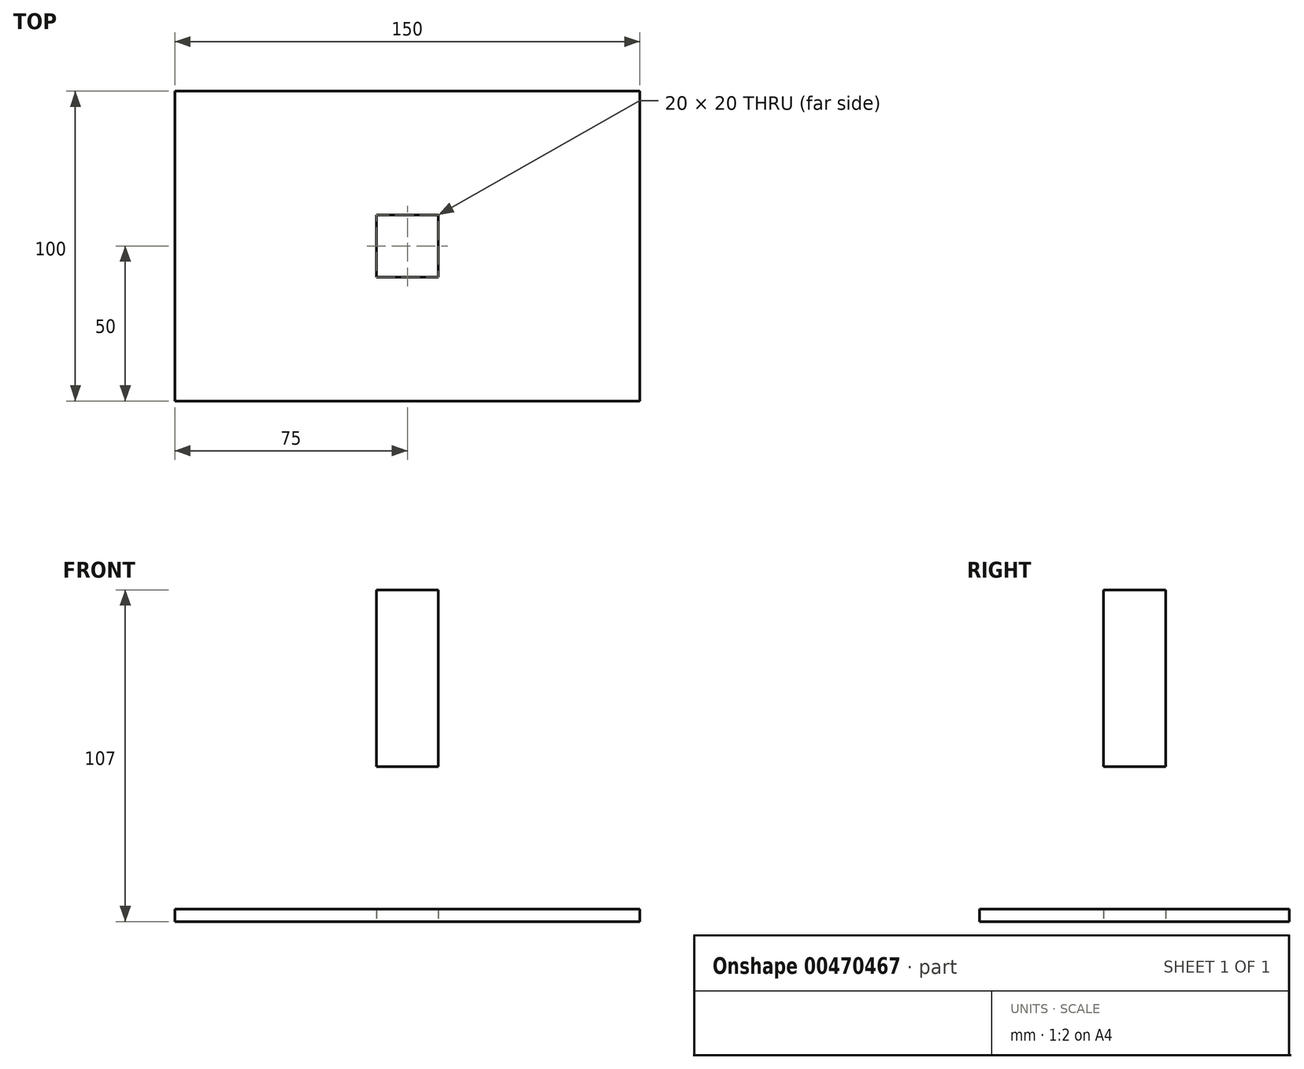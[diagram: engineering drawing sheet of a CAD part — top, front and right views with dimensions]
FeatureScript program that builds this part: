
annotation { "Feature Type Name" : "Feature", "Feature Type Description" : "" }
export const myFeature = defineFeature(function(context is Context, id is Id, definition is map)
    precondition{}
    {
        {
            var Q0;
            Q0=qCreatedBy(makeId("Top.planeOp"),FACE);
            var sketch = newSketch(context, id + "F0", { "sketchPlane" : qUnion([Q0])});
            skLineSegment(sketch, "E0.bottom", {"start": v(0, 0) * mm, "end": v(150, 0) * mm});
            skLineSegment(sketch, "E0.top", {"start": v(0, 100) * mm, "end": v(150, 100) * mm});
            skLineSegment(sketch, "E0.left", {"start": v(0, 0) * mm, "end": v(0, 100) * mm});
            skLineSegment(sketch, "E0.right", {"start": v(150, 0) * mm, "end": v(150, 100) * mm});
            skPoint(sketch, "E1.centerSnap0", {"position": v(0, 50) * mm});
            skPoint(sketch, "E1.centerSnap1", {"position": v(75, 0) * mm});
            skLineSegment(sketch, "E2.bottom", {"start": v(85, 60) * mm, "end": v(65, 60) * mm});
            skLineSegment(sketch, "E2.top", {"start": v(85, 40) * mm, "end": v(65, 40) * mm});
            skLineSegment(sketch, "E2.left", {"start": v(85, 60) * mm, "end": v(85, 40) * mm});
            skLineSegment(sketch, "E2.right", {"start": v(65, 60) * mm, "end": v(65, 40) * mm});
            skPoint(sketch, "E2.middle", {"position": v(75, 50) * mm});
            skPoint(sketch, "E2.middle.positionSnap0", {"position": v(75, 100) * mm});
            skPoint(sketch, "E2.centerSnap0", {"position": v(75, 100) * mm});
            skSolve(sketch);
        }
        {
            var Q0;
            Q0=makeQuery(id+"F0.imprint","IMPRINT",FACE,{"disambiguationData":[TD([[makeQuery(id+"F0.imprint","IMPRINT",EDGE,{"derivedFrom":sQuery(id+"F0.wireOp",EDGE,"E0.bottom")}),1.0]])]});
            extrude(context, id + "F1", {"entities" : qUnion([Q0]), "depth" : 4 * mm});
        }
        {
            var Q0;
            Q0=qCreatedBy(makeId("Top.planeOp"),FACE);
            cPlane(context, id + "F2", {"entities" : qUnion([Q0]), "cplaneType" : CPlaneType.OFFSET, "offset" : 50 * mm, "width" : 150 * mm, "height" : 150 * mm});
        }
        {
            var Q0;
            Q0=qCreatedBy(id+"F2.planeOp",FACE);
            var sketch = newSketch(context, id + "F3", { "sketchPlane" : qUnion([Q0])});
            skPoint(sketch, "E3.0", {"position": v(65, 60) * mm});
            skPoint(sketch, "E4.0", {"position": v(85, 40) * mm});
            skLineSegment(sketch, "E5.bottom", {"start": v(65, 60) * mm, "end": v(85, 60) * mm});
            skLineSegment(sketch, "E5.top", {"start": v(65, 40) * mm, "end": v(85, 40) * mm});
            skLineSegment(sketch, "E5.left", {"start": v(65, 60) * mm, "end": v(65, 40) * mm});
            skLineSegment(sketch, "E5.right", {"start": v(85, 60) * mm, "end": v(85, 40) * mm});
            skSolve(sketch);
        }
        {
            var Q0;
            Q0=makeQuery(id+"F3.imprint","IMPRINT",FACE,{"disambiguationData":[TD([[makeQuery(id+"F3.imprint","IMPRINT",EDGE,{"derivedFrom":sQuery(id+"F3.wireOp",EDGE,"E5.bottom")}),-1.0]])]});
            extrude(context, id + "F4", {"entities" : qUnion([Q0]), "depth" : 57 * mm});
        }
    });
